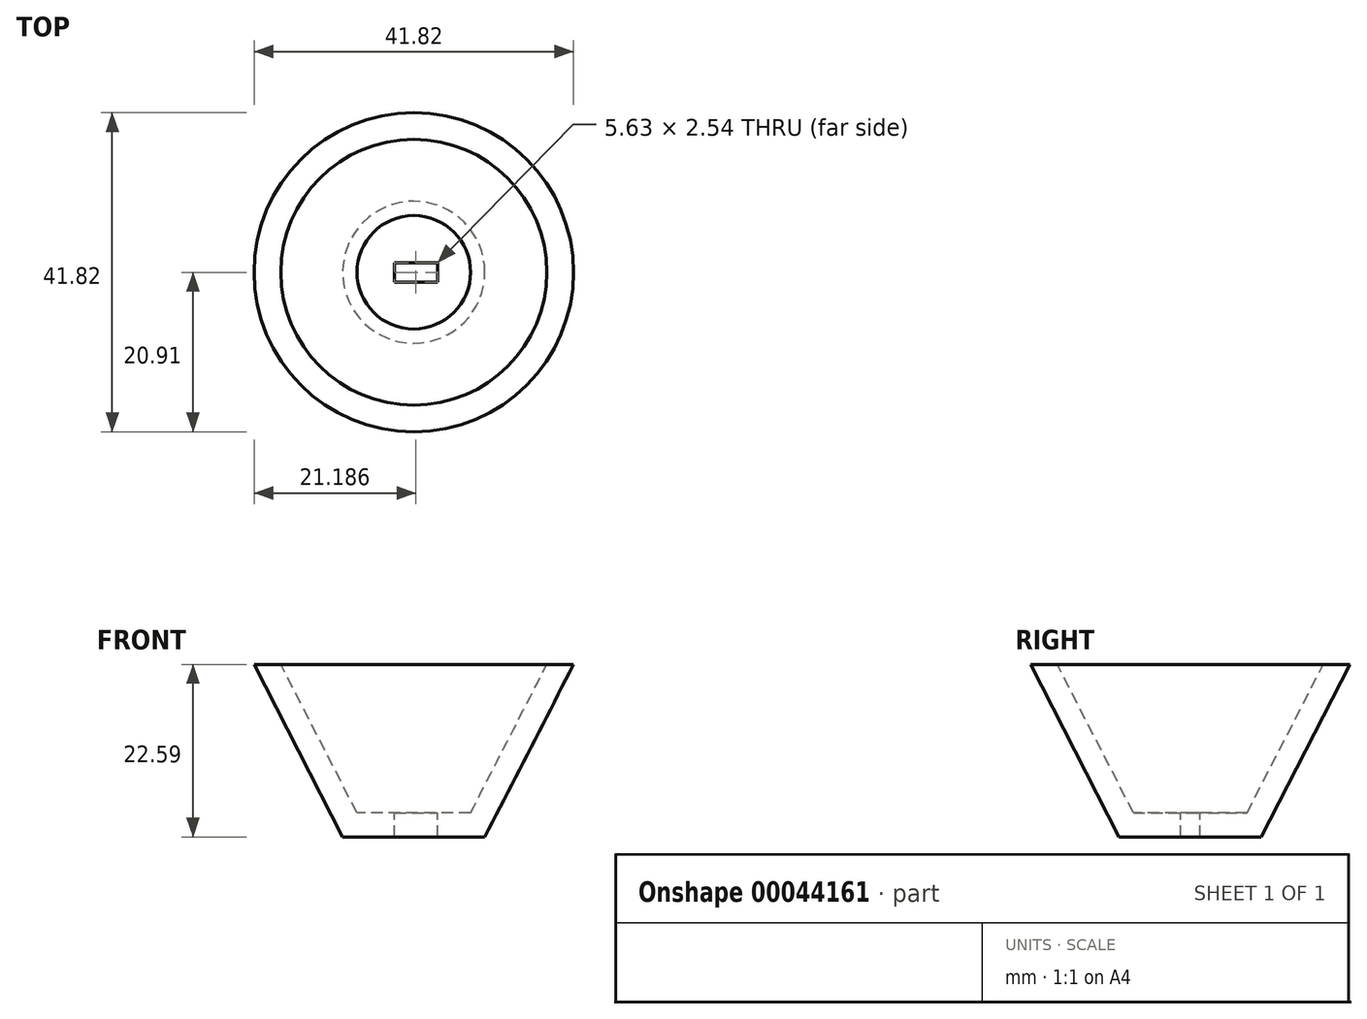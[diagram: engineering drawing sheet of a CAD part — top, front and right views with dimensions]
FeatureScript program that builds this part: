
annotation { "Feature Type Name" : "Feature", "Feature Type Description" : "" }
export const myFeature = defineFeature(function(context is Context, id is Id, definition is map)
    precondition{}
    {
        {
            var Q0;
            Q0=qCreatedBy(makeId("Front.planeOp"),FACE);
            var sketch = newSketch(context, id + "F0", { "sketchPlane" : qUnion([Q0])});
            skLineSegment(sketch, "E0", {"start": v(0, 0) * mm, "end": v(-9.3, 0) * mm});
            skLineSegment(sketch, "E1", {"start": v(-9.3, 0) * mm, "end": v(-20.91, 22.6) * mm});
            skLineSegment(sketch, "E2", {"start": v(-20.91, 22.6) * mm, "end": v(-17.41, 22.6) * mm});
            skLineSegment(sketch, "E3", {"start": v(-17.41, 22.6) * mm, "end": v(-7.43, 3.17) * mm});
            skLineSegment(sketch, "E4", {"start": v(-7.43, 3.18) * mm, "end": v(0, 3.18) * mm});
            skLineSegment(sketch, "E5", {"start": v(0, 3.18) * mm, "end": v(0, 0) * mm});
            skSolve(sketch);
        }
        {
            var Q0;
            Q0=makeQuery(id+"F0.imprint","IMPRINT",FACE,{"disambiguationData":[TD([[makeQuery(id+"F0.imprint","IMPRINT",EDGE,{"derivedFrom":sQuery(id+"F0.wireOp",EDGE,"E0")}),-1.0]])]});
            var Q1;
            Q1=sQuery(id+"F0.wireOp",EDGE,"E5");
            revolve(context, id + "F1", {"entities" : qUnion([Q0]), "axis" : qUnion([Q1]), "revolveType" : RevolveType.FULL});
        }
        {
            var Q0;
            Q0=makeQuery(id+"F1.opRevolve","SWEPT_FACE",FACE,{"disambiguationData":[OSD([sQuery(id+"F0.wireOp",EDGE,"E4")])]});
            var sketch = newSketch(context, id + "F2", { "sketchPlane" : qUnion([Q0])});
            skLineSegment(sketch, "E6.bottom", {"start": v(-2.54, 1.27) * mm, "end": v(3.1, 1.27) * mm});
            skLineSegment(sketch, "E6.top", {"start": v(-2.54, -1.27) * mm, "end": v(3.1, -1.27) * mm});
            skLineSegment(sketch, "E6.left", {"start": v(-2.54, 1.27) * mm, "end": v(-2.54, -1.27) * mm});
            skLineSegment(sketch, "E6.right", {"start": v(3.1, 1.27) * mm, "end": v(3.1, -1.27) * mm});
            skSolve(sketch);
        }
        {
            var Q0;
            Q0=makeQuery(id+"F2.imprint","IMPRINT",FACE,{"disambiguationData":[TD([[makeQuery(id+"F2.imprint","IMPRINT",EDGE,{"derivedFrom":sQuery(id+"F2.wireOp",EDGE,"E6.bottom")}),-1.0]])]});
            extrude(context, id + "F3", {"entities" : qUnion([Q0]), "operationType" : NewBodyOperationType.REMOVE, "oppositeDirection" : true, "depth" : 25.4 * mm});
        }
    });
